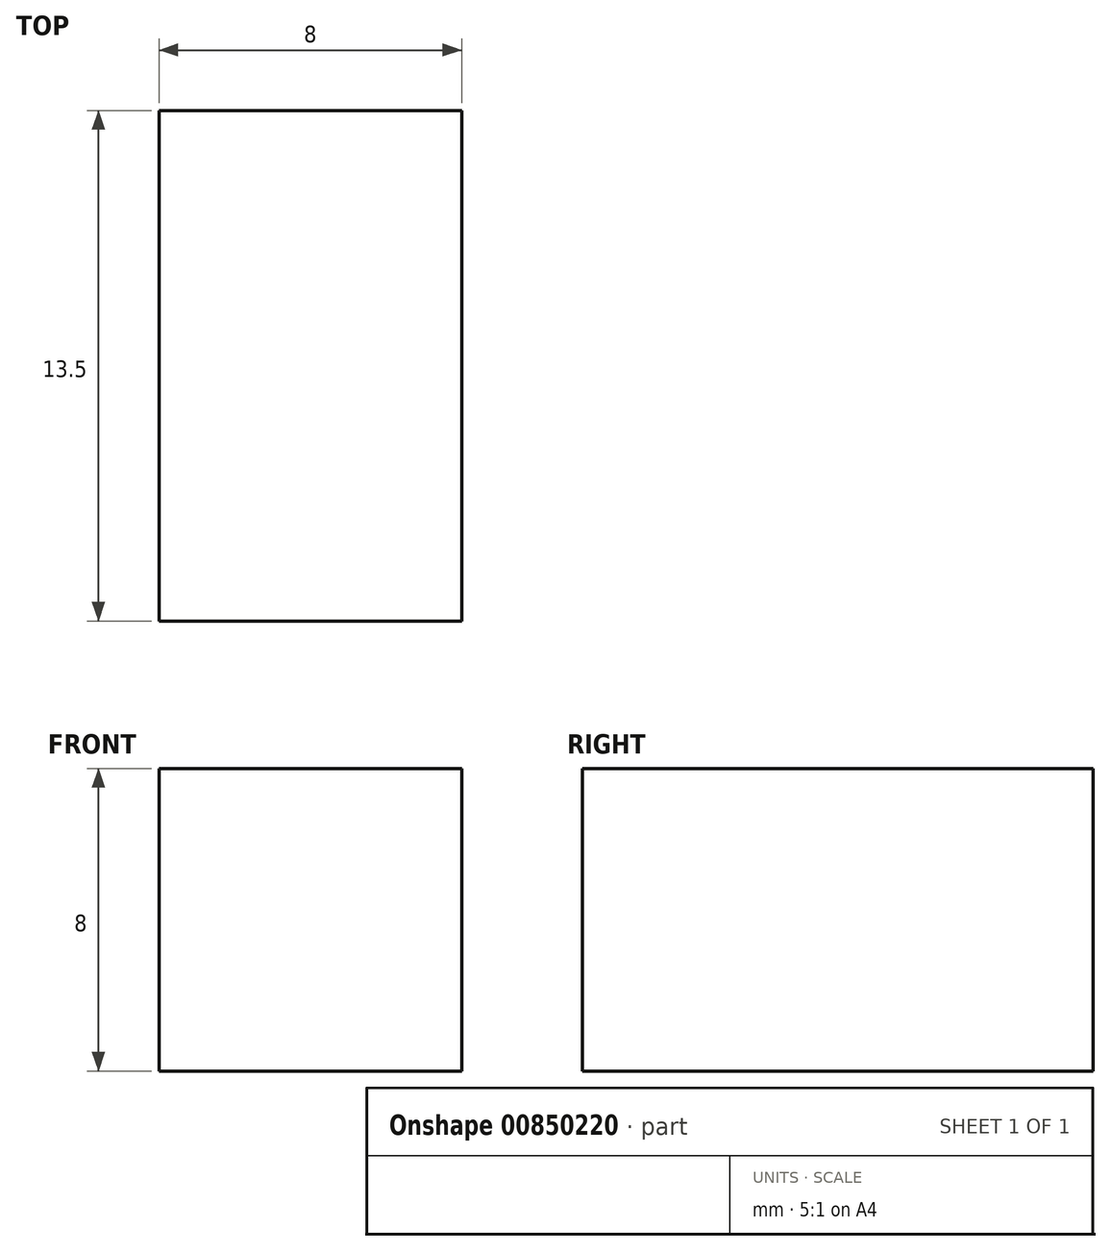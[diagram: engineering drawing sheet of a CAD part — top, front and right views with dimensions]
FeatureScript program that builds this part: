
annotation { "Feature Type Name" : "Feature", "Feature Type Description" : "" }
export const myFeature = defineFeature(function(context is Context, id is Id, definition is map)
    precondition{}
    {
        {
            var Q0;
            Q0=qCreatedBy(makeId("Front.planeOp"),FACE);
            var sketch = newSketch(context, id + "F0", { "sketchPlane" : qUnion([Q0])});
            skLineSegment(sketch, "E0.bottom", {"start": v(4, 4) * mm, "end": v(-4, 4) * mm});
            skLineSegment(sketch, "E0.top", {"start": v(4, -4) * mm, "end": v(-4, -4) * mm});
            skLineSegment(sketch, "E0.left", {"start": v(4, 4) * mm, "end": v(4, -4) * mm});
            skLineSegment(sketch, "E0.right", {"start": v(-4, 4) * mm, "end": v(-4, -4) * mm});
            skPoint(sketch, "E0.middle", {"position": v(0, 0) * mm});
            skSolve(sketch);
        }
        {
            var Q0;
            Q0 = qSketchRegion(id + "F0", true);
            extrude(context, id + "F1", {"entities" : qUnion([Q0]), "depth" : 13.5 * mm, "offsetDistance" : 25 * mm});
        }
    });
